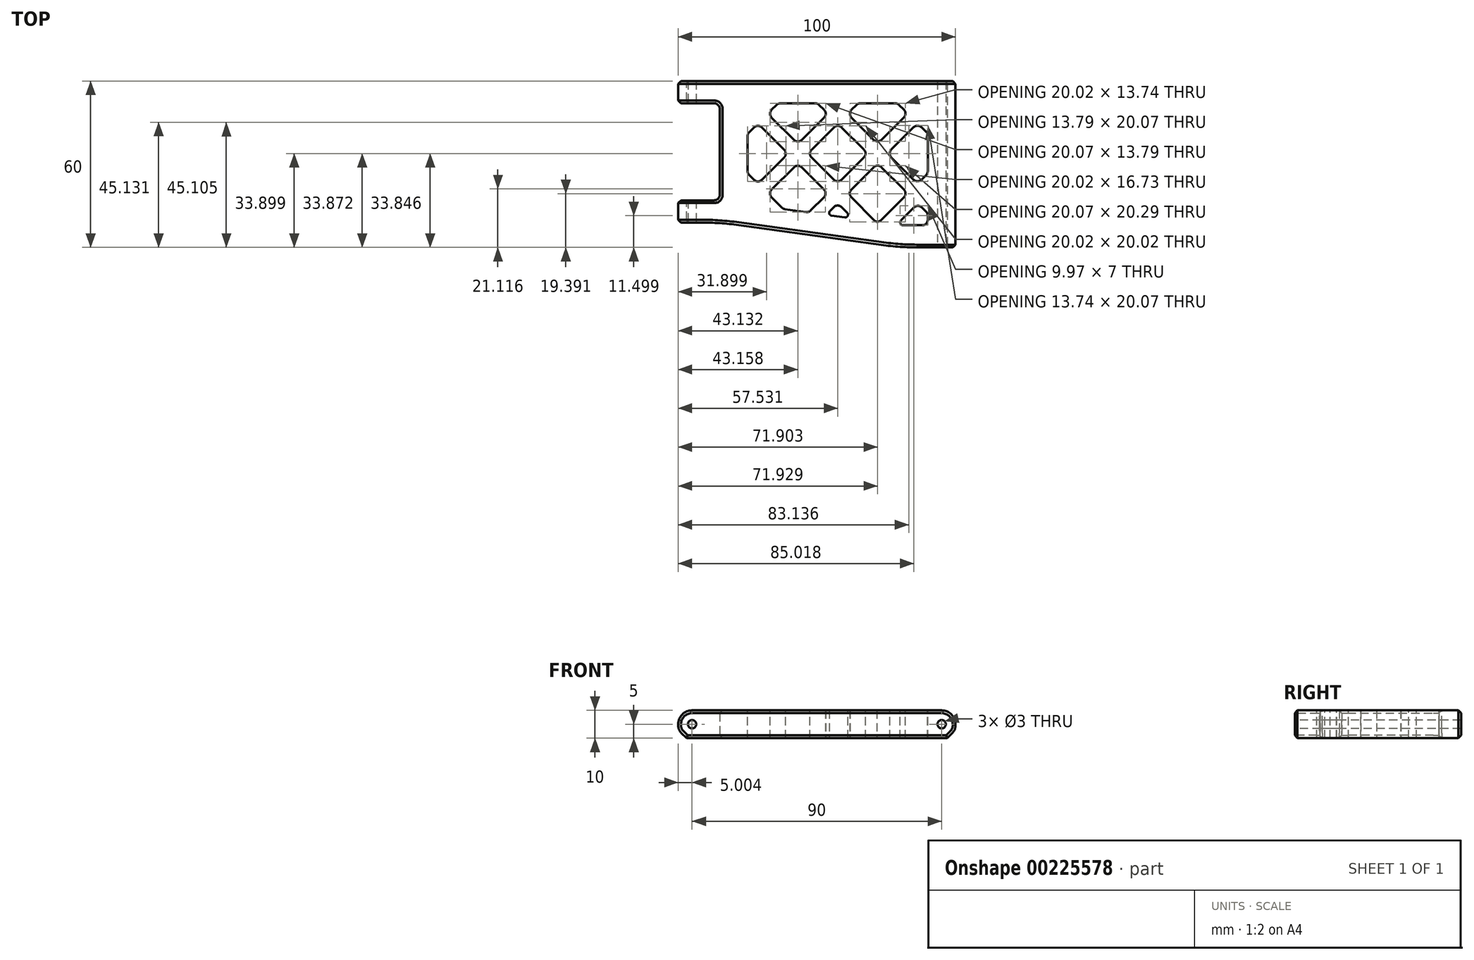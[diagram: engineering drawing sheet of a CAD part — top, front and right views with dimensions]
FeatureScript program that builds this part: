
annotation { "Feature Type Name" : "Feature", "Feature Type Description" : "" }
export const myFeature = defineFeature(function(context is Context, id is Id, definition is map)
    precondition{}
    {
        {
            var Q0;
            Q0=qCreatedBy(makeId("Top.planeOp"),FACE);
            var sketch = newSketch(context, id + "F0", { "sketchPlane" : qUnion([Q0])});
            skLineSegment(sketch, "E0", {"start": v(-37.98, 25.5) * mm, "end": v(-37.98, 17.5) * mm});
            skLineSegment(sketch, "E1", {"start": v(-37.98, 17.5) * mm, "end": v(-22.98, 17.5) * mm});
            skLineSegment(sketch, "E2", {"start": v(-22.98, 17.5) * mm, "end": v(-22.98, -17.5) * mm});
            skLineSegment(sketch, "E3", {"start": v(-22.98, -17.5) * mm, "end": v(-37.98, -17.5) * mm});
            skLineSegment(sketch, "E4", {"start": v(-37.98, -17.5) * mm, "end": v(-37.98, -25.5) * mm});
            skLineSegment(sketch, "E5", {"start": v(42.02, -34.5) * mm, "end": v(62.02, -34.5) * mm});
            skLineSegment(sketch, "E6", {"start": v(62.02, -34.5) * mm, "end": v(62.02, 25.5) * mm});
            skLineSegment(sketch, "E7", {"start": v(-37.98, -25.5) * mm, "end": v(-22.98, -25.5) * mm});
            skLineSegment(sketch, "E8", {"start": v(-22.98, -25.5) * mm, "end": v(42.02, -34.5) * mm});
            skLineSegment(sketch, "E9", {"start": v(-37.98, 25.5) * mm, "end": v(62.02, 25.5) * mm});
            skSolve(sketch);
        }
        {
            var Q0;
            Q0=makeQuery(id+"F0.imprint","IMPRINT",FACE,{"disambiguationData":[TD([[makeQuery(id+"F0.imprint","IMPRINT",EDGE,{"derivedFrom":sQuery(id+"F0.wireOp",EDGE,"E0")}),1.0]])]});
            extrude(context, id + "F1", {"entities" : qUnion([Q0]), "depth" : 10 * mm});
        }
        {
            var Q0;
            Q0=makeQuery(id+"F1.opExtrude","SWEPT_FACE",FACE,{"disambiguationData":[OSD([sQuery(id+"F0.wireOp",EDGE,"E7")])]});
            var sketch = newSketch(context, id + "F2", { "sketchPlane" : qUnion([Q0])});
            skCircle(sketch, "E10", {"center": v(-32.98, 5) * mm, "radius": 1.5 * mm});
            skPoint(sketch, "E10.centerSnap0", {"position": v(-22.98, 5) * mm});
            skSolve(sketch);
        }
        {
            var Q0;
            Q0=makeQuery(id+"F2.imprint","IMPRINT",FACE,{"disambiguationData":[TD([[makeQuery(id+"F2.imprint","IMPRINT",EDGE,{"derivedFrom":sQuery(id+"F2.wireOp",EDGE,"E10")}),1.0]])]});
            extrude(context, id + "F3", {"entities" : qUnion([Q0]), "operationType" : NewBodyOperationType.REMOVE, "endBound" : BoundingType.THROUGH_ALL, "oppositeDirection" : true, "depth" : 25 * mm});
        }
        {
            var Q0;
            Q0=makeQuery(id+"F1.opExtrude","CAP_FACE",FACE,{"disambiguationData":[OSD([sQuery(id+"F0.wireOp",EDGE,"E0"),sQuery(id+"F0.wireOp",EDGE,"E1"),sQuery(id+"F0.wireOp",EDGE,"E2"),sQuery(id+"F0.wireOp",EDGE,"E3"),sQuery(id+"F0.wireOp",EDGE,"E4"),sQuery(id+"F0.wireOp",EDGE,"E5"),sQuery(id+"F0.wireOp",EDGE,"E6"),sQuery(id+"F0.wireOp",EDGE,"BW3EDbzS-hKzO-ugTP-luI4-p5LjhiECR8vJ"),sQuery(id+"F0.wireOp",EDGE,"E7"),sQuery(id+"F0.wireOp",EDGE,"E8"),sQuery(id+"F0.wireOp",EDGE,"IeXmWBpi-uHs9-jreI-dXUk-5NaH1hiPgvdm"),sQuery(id+"F0.wireOp",EDGE,"tAyTVOHC-oCO1-Ys3H-gt9h-ad5hlT6EXF9F")])],"isStart":false});
            var sketch = newSketch(context, id + "F4", { "sketchPlane" : qUnion([Q0])});
            skLineSegment(sketch, "E11", {"start": v(-12.98, 17.5) * mm, "end": v(-12.98, -18.8) * mm});
            skLineSegment(sketch, "E12", {"start": v(-12.98, -18.8) * mm, "end": v(42.58, -26.5) * mm});
            skLineSegment(sketch, "E13", {"start": v(42.58, -26.5) * mm, "end": v(52.02, -26.5) * mm});
            skLineSegment(sketch, "E14", {"start": v(52.02, -26.5) * mm, "end": v(52.02, 17.5) * mm});
            skLineSegment(sketch, "E15", {"start": v(52.02, 17.5) * mm, "end": v(-12.98, 17.5) * mm});
            skLineSegment(sketch, "E16", {"start": v(48.49, 17.5) * mm, "end": v(9.12, -21.87) * mm});
            skLineSegment(sketch, "E17", {"start": v(52.02, 13.96) * mm, "end": v(15.33, -22.73) * mm});
            skLineSegment(sketch, "E18", {"start": v(-12.98, 13.96) * mm, "end": v(25.06, -24.08) * mm});
            skLineSegment(sketch, "E19", {"start": v(-9.44, 17.5) * mm, "end": v(33.27, -25.21) * mm});
            skLineSegment(sketch, "E20", {"start": v(-9.87, -19.24) * mm, "end": v(26.87, 17.5) * mm});
            skLineSegment(sketch, "E21", {"start": v(-12.98, -15.27) * mm, "end": v(19.8, 17.5) * mm});
            skLineSegment(sketch, "E22", {"start": v(52.02, -22.24) * mm, "end": v(12.29, 17.5) * mm});
            skLineSegment(sketch, "E23", {"start": v(52.02, -15.17) * mm, "end": v(19.36, 17.5) * mm});
            skLineSegment(sketch, "E24", {"start": v(-12.98, -7.76) * mm, "end": v(-0.15, -20.58) * mm});
            skLineSegment(sketch, "E25", {"start": v(-8.36, -19.45) * mm, "end": v(-12.98, -14.83) * mm});
            skLineSegment(sketch, "E26", {"start": v(41.08, 17.5) * mm, "end": v(52.02, 6.56) * mm});
            skLineSegment(sketch, "E27", {"start": v(44.79, -15) * mm, "end": v(34.42, -25.37) * mm});
            skLineSegment(sketch, "E28", {"start": v(44.79, -15) * mm, "end": v(52.02, -7.76) * mm});
            skLineSegment(sketch, "E29", {"start": v(40.87, -26.26) * mm, "end": v(52.02, -15.1) * mm});
            skLineSegment(sketch, "E30", {"start": v(-1.93, 17.5) * mm, "end": v(-12.98, 6.45) * mm});
            skSolve(sketch);
        }
        {
            var Q0;
            {var subQ0=sQuery(id+"F4.wireOp",EDGE,"E23");var subQ1=sQuery(id+"F4.wireOp",EDGE,"E14");var subQ2=makeQuery(id+"F4.imprint","INTERSECT",VERTEX,{"derivedFrom":[subQ1,subQ0]});Q0=makeQuery(id+"F4.imprint","IMPRINT",FACE,{"disambiguationData":[TD([[makeQuery(id+"F4.imprint","IMPRINT",EDGE,{"disambiguationData":[TD([[subQ2,-1.0]])],"derivedFrom":subQ1}),1.0]])]});}
            var Q1;
            {var subQ1=sQuery(id+"F4.wireOp",EDGE,"E13");Q1=makeQuery(id+"F4.imprint","IMPRINT",FACE,{"disambiguationData":[TD([[makeQuery(id+"F4.imprint","IMPRINT",EDGE,{"derivedFrom":subQ1}),1.0]])]});}
            var Q2;
            {var subQ0=sQuery(id+"F4.wireOp",EDGE,"E17");var subQ1=sQuery(id+"F4.wireOp",EDGE,"E12");var subQ2=makeQuery(id+"F4.imprint","INTERSECT",VERTEX,{"derivedFrom":[subQ1,subQ0]});Q2=makeQuery(id+"F4.imprint","IMPRINT",FACE,{"disambiguationData":[TD([[makeQuery(id+"F4.imprint","IMPRINT",EDGE,{"disambiguationData":[TD([[subQ2,-1.0]])],"derivedFrom":subQ1}),1.0]])]});}
            var Q3;
            {var subQ0=sQuery(id+"F4.wireOp",EDGE,"E22");var subQ1=sQuery(id+"F4.wireOp",EDGE,"E16");var subQ2=makeQuery(id+"F4.imprint","INTERSECT",VERTEX,{"derivedFrom":[subQ1,subQ0]});Q3=makeQuery(id+"F4.imprint","IMPRINT",FACE,{"disambiguationData":[TD([[makeQuery(id+"F4.imprint","IMPRINT",EDGE,{"disambiguationData":[TD([[subQ2,-1.0]])],"derivedFrom":subQ1}),-1.0]])]});}
            var Q4;
            {var subQ5=sQuery(id+"F4.wireOp",EDGE,"E16");var subQ7=sQuery(id+"F4.wireOp",EDGE,"E12");var subQ8=makeQuery(id+"F4.imprint","INTERSECT",VERTEX,{"derivedFrom":[subQ7,subQ5]});Q4=makeQuery(id+"F4.imprint","IMPRINT",FACE,{"disambiguationData":[TD([[makeQuery(id+"F4.imprint","IMPRINT",EDGE,{"disambiguationData":[TD([[subQ8,1.0]])],"derivedFrom":subQ7}),1.0]])]});}
            var Q5;
            {var subQ0=sQuery(id+"F4.wireOp",EDGE,"E24");var subQ1=sQuery(id+"F4.wireOp",EDGE,"E11");var subQ2=makeQuery(id+"F4.imprint","INTERSECT",VERTEX,{"derivedFrom":[subQ1,subQ0]});Q5=makeQuery(id+"F4.imprint","IMPRINT",FACE,{"disambiguationData":[TD([[makeQuery(id+"F4.imprint","IMPRINT",EDGE,{"disambiguationData":[TD([[subQ2,1.0]])],"derivedFrom":subQ1}),1.0]])]});}
            var Q6;
            {var subQ0=sQuery(id+"F4.wireOp",EDGE,"E22");var subQ1=sQuery(id+"F4.wireOp",EDGE,"E15");var subQ2=makeQuery(id+"F4.imprint","INTERSECT",VERTEX,{"derivedFrom":[subQ1,subQ0]});Q6=makeQuery(id+"F4.imprint","IMPRINT",FACE,{"disambiguationData":[TD([[makeQuery(id+"F4.imprint","IMPRINT",EDGE,{"disambiguationData":[TD([[subQ2,-1.0]])],"derivedFrom":subQ1}),1.0]])]});}
            var Q7;
            {var subQ0=sQuery(id+"F4.wireOp",EDGE,"E20");var subQ1=sQuery(id+"F4.wireOp",EDGE,"E15");var subQ2=makeQuery(id+"F4.imprint","INTERSECT",VERTEX,{"derivedFrom":[subQ1,subQ0]});Q7=makeQuery(id+"F4.imprint","IMPRINT",FACE,{"disambiguationData":[TD([[makeQuery(id+"F4.imprint","IMPRINT",EDGE,{"disambiguationData":[TD([[subQ2,1.0]])],"derivedFrom":subQ1}),1.0]])]});}
            var Q8;
            {var subQ0=sQuery(id+"F4.wireOp",EDGE,"E26");var subQ1=sQuery(id+"F4.wireOp",EDGE,"E14");var subQ2=makeQuery(id+"F4.imprint","INTERSECT",VERTEX,{"derivedFrom":[subQ1,subQ0]});Q8=makeQuery(id+"F4.imprint","IMPRINT",FACE,{"disambiguationData":[TD([[makeQuery(id+"F4.imprint","IMPRINT",EDGE,{"disambiguationData":[TD([[subQ2,1.0]])],"derivedFrom":subQ1}),1.0]])]});}
            var Q9;
            {var subQ5=sQuery(id+"F4.wireOp",EDGE,"E27");Q9=makeQuery(id+"F4.imprint","IMPRINT",FACE,{"disambiguationData":[TD([[makeQuery(id+"F4.imprint","IMPRINT",EDGE,{"derivedFrom":subQ5}),-1.0]])]});}
            var Q10;
            Q10=makeQuery(id+"F1.opExtrude","CAP_FACE",FACE,{"disambiguationData":[OSD([sQuery(id+"F0.wireOp",EDGE,"E0"),sQuery(id+"F0.wireOp",EDGE,"E1"),sQuery(id+"F0.wireOp",EDGE,"E2"),sQuery(id+"F0.wireOp",EDGE,"E3"),sQuery(id+"F0.wireOp",EDGE,"E4"),sQuery(id+"F0.wireOp",EDGE,"E5"),sQuery(id+"F0.wireOp",EDGE,"E6"),sQuery(id+"F0.wireOp",EDGE,"BW3EDbzS-hKzO-ugTP-luI4-p5LjhiECR8vJ"),sQuery(id+"F0.wireOp",EDGE,"E7"),sQuery(id+"F0.wireOp",EDGE,"E8"),sQuery(id+"F0.wireOp",EDGE,"IeXmWBpi-uHs9-jreI-dXUk-5NaH1hiPgvdm"),sQuery(id+"F0.wireOp",EDGE,"tAyTVOHC-oCO1-Ys3H-gt9h-ad5hlT6EXF9F")])],"isStart":true});
            extrude(context, id + "F5", {"entities" : qUnion([Q0, Q1, Q2, Q3, Q4, Q5, Q6, Q7, Q8, Q9]), "operationType" : NewBodyOperationType.REMOVE, "endBound" : BoundingType.UP_TO_SURFACE, "oppositeDirection" : true, "endBoundEntityFace" : qUnion([Q10]), "depth" : 25 * mm});
        }
        {
            var Q0;
            Q0=makeQuery(id+"F5.boolean.opBoolean","COPY",EDGE,{"derivedFrom":makeQuery(id+"F5.opExtrude","SWEPT_EDGE",EDGE,{"disambiguationData":[OSD([sQuery(id+"F4.wireOp",EDGE,"ZaEVg3SC-WDdr-0N1g-1CIV-3GaaaMJlVjN2"),sQuery(id+"F4.wireOp",EDGE,"i1amWwtg-wsxe-Ib75-jeaG-wsJk5hMrqHFT")])]})});
            var Q1;
            Q1=makeQuery(id+"F5.boolean.opBoolean","COPY",EDGE,{"derivedFrom":makeQuery(id+"F5.opExtrude","SWEPT_EDGE",EDGE,{"disambiguationData":[OSD([sQuery(id+"F4.wireOp",EDGE,"lIiY8wG4-uOwu-ETyX-0Y9X-0NFaVeheTsr8"),sQuery(id+"F4.wireOp",EDGE,"ifF4ALYo-uRmX-vEyd-hC4g-coADlhuvd4ly")])]})});
            var Q2;
            Q2=makeQuery(id+"F5.boolean.opBoolean","COPY",EDGE,{"derivedFrom":makeQuery(id+"F5.opExtrude","SWEPT_EDGE",EDGE,{"disambiguationData":[OSD([sQuery(id+"F4.wireOp",EDGE,"KTq638T6-onXi-3Qut-dIgx-5TcDHjVjb5bx"),sQuery(id+"F4.wireOp",EDGE,"lIiY8wG4-uOwu-ETyX-0Y9X-0NFaVeheTsr8")])]})});
            var Q3;
            Q3=makeQuery(id+"F5.boolean.opBoolean","COPY",EDGE,{"derivedFrom":makeQuery(id+"F5.opExtrude","SWEPT_EDGE",EDGE,{"disambiguationData":[OSD([sQuery(id+"F4.wireOp",EDGE,"adEcOkNO-EfV1-quEy-cv4m-vqoQPHR0sBr5"),sQuery(id+"F4.wireOp",EDGE,"FiieaGRp-roSN-Qhw9-YWAH-qJouDKNjpClN")])]})});
            var Q4;
            Q4=makeQuery(id+"F5.boolean.opBoolean","COPY",EDGE,{"derivedFrom":makeQuery(id+"F5.opExtrude","SWEPT_EDGE",EDGE,{"disambiguationData":[OSD([sQuery(id+"F4.wireOp",EDGE,"fQXT7rkZ-4DuX-Y0vK-KIZa-FyNlYHUYCe49"),sQuery(id+"F4.wireOp",EDGE,"i1amWwtg-wsxe-Ib75-jeaG-wsJk5hMrqHFT"),sQuery(id+"F4.wireOp",EDGE,"FiieaGRp-roSN-Qhw9-YWAH-qJouDKNjpClN")])]})});
            var Q5;
            Q5=makeQuery(id+"F5.boolean.opBoolean","COPY",EDGE,{"derivedFrom":makeQuery(id+"F5.opExtrude","SWEPT_EDGE",EDGE,{"disambiguationData":[OSD([sQuery(id+"F4.wireOp",EDGE,"fQXT7rkZ-4DuX-Y0vK-KIZa-FyNlYHUYCe49"),sQuery(id+"F4.wireOp",EDGE,"6CixbW05-UBlS-MQcj-7FzB-Ca1LVtebaFVZ")])]})});
            var Q6;
            Q6=makeQuery(id+"F5.boolean.opBoolean","COPY",EDGE,{"derivedFrom":makeQuery(id+"F5.opExtrude","SWEPT_EDGE",EDGE,{"disambiguationData":[OSD([sQuery(id+"F4.wireOp",EDGE,"lIiY8wG4-uOwu-ETyX-0Y9X-0NFaVeheTsr8"),sQuery(id+"F4.wireOp",EDGE,"fQXT7rkZ-4DuX-Y0vK-KIZa-FyNlYHUYCe49")])]})});
            var Q7;
            Q7=makeQuery(id+"F5.boolean.opBoolean","COPY",EDGE,{"derivedFrom":makeQuery(id+"F5.opExtrude","SWEPT_EDGE",EDGE,{"disambiguationData":[OSD([sQuery(id+"F4.wireOp",EDGE,"lIiY8wG4-uOwu-ETyX-0Y9X-0NFaVeheTsr8"),sQuery(id+"F4.wireOp",EDGE,"FiieaGRp-roSN-Qhw9-YWAH-qJouDKNjpClN")])]})});
            var Q8;
            Q8=makeQuery(id+"F5.boolean.opBoolean","COPY",EDGE,{"derivedFrom":makeQuery(id+"F5.opExtrude","SWEPT_EDGE",EDGE,{"disambiguationData":[OSD([sQuery(id+"F4.wireOp",EDGE,"QQoZa2y4-lnB9-MFLh-E48C-Qh8QXVeHaOTo"),sQuery(id+"F4.wireOp",EDGE,"6CixbW05-UBlS-MQcj-7FzB-Ca1LVtebaFVZ")])]})});
            var Q9;
            Q9=makeQuery(id+"F5.boolean.opBoolean","COPY",EDGE,{"derivedFrom":makeQuery(id+"F5.opExtrude","SWEPT_EDGE",EDGE,{"disambiguationData":[OSD([sQuery(id+"F4.wireOp",EDGE,"PUbkOMFc-aEfS-HhHo-NWSC-wt2yRkt3aVop"),sQuery(id+"F4.wireOp",EDGE,"adEcOkNO-EfV1-quEy-cv4m-vqoQPHR0sBr5")])]})});
            var Q10;
            Q10=makeQuery(id+"F5.boolean.opBoolean","COPY",EDGE,{"derivedFrom":makeQuery(id+"F5.opExtrude","SWEPT_EDGE",EDGE,{"disambiguationData":[OSD([sQuery(id+"F4.wireOp",EDGE,"u151USCK-d2Jm-vOpM-AoZG-Gq13jmKxo3bC"),sQuery(id+"F4.wireOp",EDGE,"ZaEVg3SC-WDdr-0N1g-1CIV-3GaaaMJlVjN2")])]})});
            var Q11;
            Q11=makeQuery(id+"F5.boolean.opBoolean","COPY",EDGE,{"derivedFrom":makeQuery(id+"F5.opExtrude","SWEPT_EDGE",EDGE,{"disambiguationData":[OSD([sQuery(id+"F4.wireOp",EDGE,"PUbkOMFc-aEfS-HhHo-NWSC-wt2yRkt3aVop"),sQuery(id+"F4.wireOp",EDGE,"CK30QNie-qYM8-a8fS-8cOY-rL2En2E0fWi0")])]})});
            var Q12;
            Q12=makeQuery(id+"F5.boolean.opBoolean","COPY",EDGE,{"derivedFrom":makeQuery(id+"F5.opExtrude","SWEPT_EDGE",EDGE,{"disambiguationData":[OSD([sQuery(id+"F4.wireOp",EDGE,"QQoZa2y4-lnB9-MFLh-E48C-Qh8QXVeHaOTo"),sQuery(id+"F4.wireOp",EDGE,"u151USCK-d2Jm-vOpM-AoZG-Gq13jmKxo3bC")])]})});
            var Q13;
            Q13=makeQuery(id+"F5.boolean.opBoolean","COPY",EDGE,{"derivedFrom":makeQuery(id+"F5.opExtrude","SWEPT_EDGE",EDGE,{"disambiguationData":[OSD([sQuery(id+"F4.wireOp",EDGE,"PUbkOMFc-aEfS-HhHo-NWSC-wt2yRkt3aVop"),sQuery(id+"F4.wireOp",EDGE,"tCY4romA-bLon-Adh6-hAWd-4SXAEG81LoxB")])]})});
            var Q14;
            Q14=makeQuery(id+"F5.boolean.opBoolean","COPY",EDGE,{"derivedFrom":makeQuery(id+"F5.opExtrude","SWEPT_EDGE",EDGE,{"disambiguationData":[OSD([sQuery(id+"F4.wireOp",EDGE,"tCY4romA-bLon-Adh6-hAWd-4SXAEG81LoxB"),sQuery(id+"F4.wireOp",EDGE,"4gVtD0sa-nhfM-sN6f-blQz-uG5Zat8Q9Qrc")])]})});
            var Q15;
            Q15=makeQuery(id+"F5.boolean.opBoolean","COPY",EDGE,{"derivedFrom":makeQuery(id+"F5.opExtrude","SWEPT_EDGE",EDGE,{"disambiguationData":[OSD([sQuery(id+"F4.wireOp",EDGE,"QQoZa2y4-lnB9-MFLh-E48C-Qh8QXVeHaOTo"),sQuery(id+"F4.wireOp",EDGE,"xG4hkh3S-L24H-y6HB-11TF-rizkPmb2XNVC")])]})});
            var Q16;
            Q16=makeQuery(id+"F5.boolean.opBoolean","COPY",EDGE,{"derivedFrom":makeQuery(id+"F5.opExtrude","SWEPT_EDGE",EDGE,{"disambiguationData":[OSD([sQuery(id+"F4.wireOp",EDGE,"u151USCK-d2Jm-vOpM-AoZG-Gq13jmKxo3bC"),sQuery(id+"F4.wireOp",EDGE,"xG4hkh3S-L24H-y6HB-11TF-rizkPmb2XNVC")])]})});
            var Q17;
            Q17=makeQuery(id+"F5.boolean.opBoolean","COPY",EDGE,{"derivedFrom":makeQuery(id+"F5.opExtrude","SWEPT_EDGE",EDGE,{"disambiguationData":[OSD([sQuery(id+"F4.wireOp",EDGE,"tCY4romA-bLon-Adh6-hAWd-4SXAEG81LoxB"),sQuery(id+"F4.wireOp",EDGE,"CK30QNie-qYM8-a8fS-8cOY-rL2En2E0fWi0"),sQuery(id+"F4.wireOp",EDGE,"ZaEVg3SC-WDdr-0N1g-1CIV-3GaaaMJlVjN2")])]})});
            var Q18;
            Q18=makeQuery(id+"F5.boolean.opBoolean","COPY",EDGE,{"derivedFrom":makeQuery(id+"F5.opExtrude","SWEPT_EDGE",EDGE,{"disambiguationData":[OSD([sQuery(id+"F4.wireOp",EDGE,"UHvlroPN-YfBx-vEqm-jT0p-LSI2mjvl9sd3"),sQuery(id+"F4.wireOp",EDGE,"4gVtD0sa-nhfM-sN6f-blQz-uG5Zat8Q9Qrc")])]})});
            var Q19;
            Q19=makeQuery(id+"F5.boolean.opBoolean","COPY",EDGE,{"derivedFrom":makeQuery(id+"F5.opExtrude","SWEPT_EDGE",EDGE,{"disambiguationData":[OSD([sQuery(id+"F4.wireOp",EDGE,"UHvlroPN-YfBx-vEqm-jT0p-LSI2mjvl9sd3"),sQuery(id+"F4.wireOp",EDGE,"tCY4romA-bLon-Adh6-hAWd-4SXAEG81LoxB")])]})});
            var Q20;
            Q20=makeQuery(id+"F1.opExtrude","SWEPT_EDGE",EDGE,{"disambiguationData":[OSD([sQuery(id+"F0.wireOp",EDGE,"E1"),sQuery(id+"F0.wireOp",EDGE,"E2")])]});
            var Q21;
            Q21=makeQuery(id+"F1.opExtrude","SWEPT_EDGE",EDGE,{"disambiguationData":[OSD([sQuery(id+"F0.wireOp",EDGE,"E2"),sQuery(id+"F0.wireOp",EDGE,"E3")])]});
            fillet(context, id + "F6", {"entities" : qUnion([Q0, Q1, Q2, Q3, Q4, Q5, Q6, Q7, Q8, Q9, Q10, Q11, Q12, Q13, Q14, Q15, Q16, Q17, Q18, Q19, Q20, Q21]), "radius" : 2 * mm, "tangentPropagation" : true, "allowEdgeOverflow" : false});
        }
        {
            var Q0;
            Q0=makeQuery(id+"F1.opExtrude","CAP_EDGE",EDGE,{"disambiguationData":[OSD([sQuery(id+"F0.wireOp",EDGE,"E0")])],"isStart":false});
            var Q1;
            Q1=makeQuery(id+"F1.opExtrude","CAP_EDGE",EDGE,{"disambiguationData":[OSD([sQuery(id+"F0.wireOp",EDGE,"E4")])],"isStart":false});
            var Q2;
            Q2=makeQuery(id+"F1.opExtrude","CAP_EDGE",EDGE,{"disambiguationData":[OSD([sQuery(id+"F0.wireOp",EDGE,"E6")])],"isStart":false});
            fillet(context, id + "F7", {"entities" : qUnion([Q0, Q1, Q2]), "radius" : 5 * mm, "tangentPropagation" : true, "allowEdgeOverflow" : false});
        }
        {
            var Q0;
            Q0=makeQuery(id+"F1.opExtrude","CAP_EDGE",EDGE,{"disambiguationData":[OSD([sQuery(id+"F0.wireOp",EDGE,"E4")])],"isStart":true});
            var Q1;
            Q1=makeQuery(id+"F1.opExtrude","CAP_EDGE",EDGE,{"disambiguationData":[OSD([sQuery(id+"F0.wireOp",EDGE,"E0")])],"isStart":true});
            var Q2;
            Q2=makeQuery(id+"F1.opExtrude","CAP_EDGE",EDGE,{"disambiguationData":[OSD([sQuery(id+"F0.wireOp",EDGE,"E6")])],"isStart":true});
            chamfer(context, id + "F8", {"entities" : qUnion([Q0, Q1, Q2]), "width" : 3 * mm, "tangentPropagation" : true});
        }
        {
            var Q0;
            {var subQ0=sQuery(id+"F0.wireOp",EDGE,"E6");Q0=makeQuery(id+"F8.opChamfer","BLEND_EDGE",EDGE,{"blendedFrom":[makeQuery(id+"F1.opExtrude","CAP_EDGE",EDGE,{"disambiguationData":[OSD([subQ0])],"isStart":true}),makeQuery(id+"F1.opExtrude","SWEPT_FACE",FACE,{"disambiguationData":[OSD([subQ0])]})],"blendedInto":[makeQuery(id+"F1.opExtrude","SWEPT_FACE",FACE,{"disambiguationData":[OSD([subQ0])]})]});}
            var Q1;
            {var subQ0=sQuery(id+"F0.wireOp",EDGE,"E4");Q1=makeQuery(id+"F8.opChamfer","BLEND_EDGE",EDGE,{"blendedFrom":[makeQuery(id+"F1.opExtrude","CAP_EDGE",EDGE,{"disambiguationData":[OSD([subQ0])],"isStart":true}),makeQuery(id+"F1.opExtrude","SWEPT_FACE",FACE,{"disambiguationData":[OSD([subQ0])]})],"blendedInto":[makeQuery(id+"F1.opExtrude","SWEPT_FACE",FACE,{"disambiguationData":[OSD([subQ0])]})]});}
            var Q2;
            {var subQ0=sQuery(id+"F0.wireOp",EDGE,"E0");Q2=makeQuery(id+"F8.opChamfer","BLEND_EDGE",EDGE,{"blendedFrom":[makeQuery(id+"F1.opExtrude","CAP_EDGE",EDGE,{"disambiguationData":[OSD([subQ0])],"isStart":true}),makeQuery(id+"F1.opExtrude","SWEPT_FACE",FACE,{"disambiguationData":[OSD([subQ0])]})],"blendedInto":[makeQuery(id+"F1.opExtrude","SWEPT_FACE",FACE,{"disambiguationData":[OSD([subQ0])]})]});}
            fillet(context, id + "F9", {"entities" : qUnion([Q0, Q1, Q2]), "radius" : 4 * mm, "tangentPropagation" : true, "allowEdgeOverflow" : false});
        }
        {
            var Q0;
            Q0=makeQuery(id+"F1.opExtrude","SWEPT_EDGE",EDGE,{"disambiguationData":[OSD([sQuery(id+"F0.wireOp",EDGE,"E7"),sQuery(id+"F0.wireOp",EDGE,"E8")])]});
            var Q1;
            Q1=makeQuery(id+"F1.opExtrude","SWEPT_EDGE",EDGE,{"disambiguationData":[OSD([sQuery(id+"F0.wireOp",EDGE,"IeXmWBpi-uHs9-jreI-dXUk-5NaH1hiPgvdm"),sQuery(id+"F0.wireOp",EDGE,"tAyTVOHC-oCO1-Ys3H-gt9h-ad5hlT6EXF9F")])]});
            var Q2;
            Q2=makeQuery(id+"F1.opExtrude","SWEPT_EDGE",EDGE,{"disambiguationData":[OSD([sQuery(id+"F0.wireOp",EDGE,"BW3EDbzS-hKzO-ugTP-luI4-p5LjhiECR8vJ"),sQuery(id+"F0.wireOp",EDGE,"tAyTVOHC-oCO1-Ys3H-gt9h-ad5hlT6EXF9F")])]});
            var Q3;
            Q3=makeQuery(id+"F1.opExtrude","SWEPT_EDGE",EDGE,{"disambiguationData":[OSD([sQuery(id+"F0.wireOp",EDGE,"E5"),sQuery(id+"F0.wireOp",EDGE,"E8")])]});
            fillet(context, id + "F10", {"entities" : qUnion([Q0, Q1, Q2, Q3]), "radius" : 100 * mm, "allowEdgeOverflow" : false});
        }
        {
            var Q0;
            Q0=makeQuery(id+"F1.opExtrude","SWEPT_FACE",FACE,{"disambiguationData":[OSD([sQuery(id+"F0.wireOp",EDGE,"E5")])]});
            var sketch = newSketch(context, id + "F11", { "sketchPlane" : qUnion([Q0])});
            skCircle(sketch, "E31", {"center": v(57.02, 5) * mm, "radius": 1.5 * mm});
            skPoint(sketch, "E31.centerSnap0", {"position": v(48.91, 5) * mm});
            skSolve(sketch);
        }
        {
            var Q0;
            Q0=makeQuery(id+"F11.imprint","IMPRINT",FACE,{"disambiguationData":[TD([[makeQuery(id+"F11.imprint","IMPRINT",EDGE,{"derivedFrom":sQuery(id+"F11.wireOp",EDGE,"E31")}),1.0]])]});
            extrude(context, id + "F12", {"entities" : qUnion([Q0]), "operationType" : NewBodyOperationType.REMOVE, "endBound" : BoundingType.THROUGH_ALL, "oppositeDirection" : true, "depth" : 25 * mm});
        }
        {
            var Q0;
            {var subQ0=sQuery(id+"F0.wireOp",EDGE,"E8");var subQ1=sQuery(id+"F0.wireOp",EDGE,"E7");Q0=makeQuery(id+"F10.opFillet","BLEND_EDGE",EDGE,{"blendedFrom":[makeQuery(id+"F1.opExtrude","SWEPT_EDGE",EDGE,{"disambiguationData":[OSD([subQ1,subQ0])]}),makeQuery(id+"F1.opExtrude","CAP_FACE",FACE,{"disambiguationData":[OSD([sQuery(id+"F0.wireOp",EDGE,"E0"),sQuery(id+"F0.wireOp",EDGE,"E1"),sQuery(id+"F0.wireOp",EDGE,"E2"),sQuery(id+"F0.wireOp",EDGE,"E3"),sQuery(id+"F0.wireOp",EDGE,"E4"),sQuery(id+"F0.wireOp",EDGE,"E5"),sQuery(id+"F0.wireOp",EDGE,"E6"),sQuery(id+"F0.wireOp",EDGE,"BW3EDbzS-hKzO-ugTP-luI4-p5LjhiECR8vJ"),subQ1,subQ0,sQuery(id+"F0.wireOp",EDGE,"IeXmWBpi-uHs9-jreI-dXUk-5NaH1hiPgvdm"),sQuery(id+"F0.wireOp",EDGE,"tAyTVOHC-oCO1-Ys3H-gt9h-ad5hlT6EXF9F")])],"isStart":false})],"blendedInto":[makeQuery(id+"F1.opExtrude","CAP_FACE",FACE,{"disambiguationData":[OSD([sQuery(id+"F0.wireOp",EDGE,"E0"),sQuery(id+"F0.wireOp",EDGE,"E1"),sQuery(id+"F0.wireOp",EDGE,"E2"),sQuery(id+"F0.wireOp",EDGE,"E3"),sQuery(id+"F0.wireOp",EDGE,"E4"),sQuery(id+"F0.wireOp",EDGE,"E5"),sQuery(id+"F0.wireOp",EDGE,"E6"),sQuery(id+"F0.wireOp",EDGE,"BW3EDbzS-hKzO-ugTP-luI4-p5LjhiECR8vJ"),subQ1,subQ0,sQuery(id+"F0.wireOp",EDGE,"IeXmWBpi-uHs9-jreI-dXUk-5NaH1hiPgvdm"),sQuery(id+"F0.wireOp",EDGE,"tAyTVOHC-oCO1-Ys3H-gt9h-ad5hlT6EXF9F")])],"isStart":false})]});}
            var Q1;
            Q1=makeQuery(id+"F1.opExtrude","CAP_EDGE",EDGE,{"disambiguationData":[OSD([sQuery(id+"F0.wireOp",EDGE,"E7")])],"isStart":true});
            var Q2;
            Q2=makeQuery(id+"F1.opExtrude","CAP_EDGE",EDGE,{"disambiguationData":[OSD([sQuery(id+"F0.wireOp",EDGE,"IeXmWBpi-uHs9-jreI-dXUk-5NaH1hiPgvdm")])],"isStart":true});
            var Q3;
            Q3=makeQuery(id+"F1.opExtrude","CAP_EDGE",EDGE,{"disambiguationData":[OSD([sQuery(id+"F0.wireOp",EDGE,"E1")])],"isStart":true});
            var Q4;
            Q4=makeQuery(id+"F1.opExtrude","CAP_EDGE",EDGE,{"disambiguationData":[OSD([sQuery(id+"F0.wireOp",EDGE,"E2")])],"isStart":false});
            var Q5;
            Q5=makeQuery(id+"F1.opExtrude","CAP_EDGE",EDGE,{"disambiguationData":[OSD([sQuery(id+"F0.wireOp",EDGE,"tAyTVOHC-oCO1-Ys3H-gt9h-ad5hlT6EXF9F")])],"isStart":false});
            chamfer(context, id + "F13", {"entities" : qUnion([Q0, Q1, Q2, Q3, Q4, Q5]), "width" : 1 * mm, "tangentPropagation" : true});
        }
        {
            var Q0;
            Q0=makeQuery(id+"F5.boolean.opBoolean","COPY",EDGE,{"derivedFrom":makeQuery(id+"F5.opExtrude","SWEPT_EDGE",EDGE,{"disambiguationData":[OSD([sQuery(id+"F4.wireOp",EDGE,"E15"),sQuery(id+"F4.wireOp",EDGE,"E30")])]})});
            var Q1;
            Q1=makeQuery(id+"F5.boolean.opBoolean","COPY",EDGE,{"derivedFrom":makeQuery(id+"F5.opExtrude","SWEPT_EDGE",EDGE,{"disambiguationData":[OSD([sQuery(id+"F4.wireOp",EDGE,"E19"),sQuery(id+"F4.wireOp",EDGE,"E30")])]})});
            var Q2;
            Q2=makeQuery(id+"F5.boolean.opBoolean","COPY",EDGE,{"derivedFrom":makeQuery(id+"F5.opExtrude","SWEPT_EDGE",EDGE,{"disambiguationData":[OSD([sQuery(id+"F4.wireOp",EDGE,"E18"),sQuery(id+"F4.wireOp",EDGE,"E30")])]})});
            var Q3;
            Q3=makeQuery(id+"F5.boolean.opBoolean","COPY",EDGE,{"derivedFrom":makeQuery(id+"F5.opExtrude","SWEPT_EDGE",EDGE,{"disambiguationData":[OSD([sQuery(id+"F4.wireOp",EDGE,"E11"),sQuery(id+"F4.wireOp",EDGE,"E30")])]})});
            var Q4;
            Q4=makeQuery(id+"F5.boolean.opBoolean","COPY",EDGE,{"derivedFrom":makeQuery(id+"F5.opExtrude","SWEPT_EDGE",EDGE,{"disambiguationData":[OSD([sQuery(id+"F4.wireOp",EDGE,"E11"),sQuery(id+"F4.wireOp",EDGE,"E24")])]})});
            var Q5;
            Q5=makeQuery(id+"F5.boolean.opBoolean","COPY",EDGE,{"derivedFrom":makeQuery(id+"F5.opExtrude","SWEPT_EDGE",EDGE,{"disambiguationData":[OSD([sQuery(id+"F4.wireOp",EDGE,"E21"),sQuery(id+"F4.wireOp",EDGE,"E24")])]})});
            var Q6;
            Q6=makeQuery(id+"F5.boolean.opBoolean","COPY",EDGE,{"derivedFrom":makeQuery(id+"F5.opExtrude","SWEPT_EDGE",EDGE,{"disambiguationData":[OSD([sQuery(id+"F4.wireOp",EDGE,"E18"),sQuery(id+"F4.wireOp",EDGE,"E21")])]})});
            var Q7;
            Q7=makeQuery(id+"F5.boolean.opBoolean","COPY",EDGE,{"derivedFrom":makeQuery(id+"F5.opExtrude","SWEPT_EDGE",EDGE,{"disambiguationData":[OSD([sQuery(id+"F4.wireOp",EDGE,"E19"),sQuery(id+"F4.wireOp",EDGE,"E21")])]})});
            var Q8;
            Q8=makeQuery(id+"F5.boolean.opBoolean","COPY",EDGE,{"derivedFrom":makeQuery(id+"F5.opExtrude","SWEPT_EDGE",EDGE,{"disambiguationData":[OSD([sQuery(id+"F4.wireOp",EDGE,"E21"),sQuery(id+"F4.wireOp",EDGE,"E22")])]})});
            var Q9;
            Q9=makeQuery(id+"F5.boolean.opBoolean","COPY",EDGE,{"derivedFrom":makeQuery(id+"F5.opExtrude","SWEPT_EDGE",EDGE,{"disambiguationData":[OSD([sQuery(id+"F4.wireOp",EDGE,"E15"),sQuery(id+"F4.wireOp",EDGE,"E22")])]})});
            var Q10;
            Q10=makeQuery(id+"F5.boolean.opBoolean","COPY",EDGE,{"derivedFrom":makeQuery(id+"F5.opExtrude","SWEPT_EDGE",EDGE,{"disambiguationData":[OSD([sQuery(id+"F4.wireOp",EDGE,"E20"),sQuery(id+"F4.wireOp",EDGE,"E24")])]})});
            var Q11;
            Q11=makeQuery(id+"F5.boolean.opBoolean","COPY",EDGE,{"derivedFrom":makeQuery(id+"F5.opExtrude","SWEPT_EDGE",EDGE,{"disambiguationData":[OSD([sQuery(id+"F4.wireOp",EDGE,"E12"),sQuery(id+"F4.wireOp",EDGE,"E24")])]})});
            var Q12;
            Q12=makeQuery(id+"F5.boolean.opBoolean","COPY",EDGE,{"derivedFrom":makeQuery(id+"F5.opExtrude","SWEPT_EDGE",EDGE,{"disambiguationData":[OSD([sQuery(id+"F4.wireOp",EDGE,"E12"),sQuery(id+"F4.wireOp",EDGE,"E16")])]})});
            var Q13;
            Q13=makeQuery(id+"F5.boolean.opBoolean","COPY",EDGE,{"derivedFrom":makeQuery(id+"F5.opExtrude","SWEPT_EDGE",EDGE,{"disambiguationData":[OSD([sQuery(id+"F4.wireOp",EDGE,"E16"),sQuery(id+"F4.wireOp",EDGE,"E18")])]})});
            var Q14;
            Q14=makeQuery(id+"F5.boolean.opBoolean","COPY",EDGE,{"derivedFrom":makeQuery(id+"F5.opExtrude","SWEPT_EDGE",EDGE,{"disambiguationData":[OSD([sQuery(id+"F4.wireOp",EDGE,"E18"),sQuery(id+"F4.wireOp",EDGE,"E20")])]})});
            var Q15;
            Q15=makeQuery(id+"F5.boolean.opBoolean","COPY",EDGE,{"derivedFrom":makeQuery(id+"F5.opExtrude","SWEPT_EDGE",EDGE,{"disambiguationData":[OSD([sQuery(id+"F4.wireOp",EDGE,"E20"),sQuery(id+"F4.wireOp",EDGE,"E22")])]})});
            var Q16;
            Q16=makeQuery(id+"F5.boolean.opBoolean","COPY",EDGE,{"derivedFrom":makeQuery(id+"F5.opExtrude","SWEPT_EDGE",EDGE,{"disambiguationData":[OSD([sQuery(id+"F4.wireOp",EDGE,"E15"),sQuery(id+"F4.wireOp",EDGE,"E20")])]})});
            var Q17;
            Q17=makeQuery(id+"F5.boolean.opBoolean","COPY",EDGE,{"derivedFrom":makeQuery(id+"F5.opExtrude","SWEPT_EDGE",EDGE,{"disambiguationData":[OSD([sQuery(id+"F4.wireOp",EDGE,"E17"),sQuery(id+"F4.wireOp",EDGE,"E22")])]})});
            var Q18;
            Q18=makeQuery(id+"F5.boolean.opBoolean","COPY",EDGE,{"derivedFrom":makeQuery(id+"F5.opExtrude","SWEPT_EDGE",EDGE,{"disambiguationData":[OSD([sQuery(id+"F4.wireOp",EDGE,"E17"),sQuery(id+"F4.wireOp",EDGE,"E26")])]})});
            var Q19;
            Q19=makeQuery(id+"F5.boolean.opBoolean","COPY",EDGE,{"derivedFrom":makeQuery(id+"F5.opExtrude","SWEPT_EDGE",EDGE,{"disambiguationData":[OSD([sQuery(id+"F4.wireOp",EDGE,"E22"),sQuery(id+"F4.wireOp",EDGE,"E29")])]})});
            var Q20;
            Q20=makeQuery(id+"F5.boolean.opBoolean","COPY",EDGE,{"derivedFrom":makeQuery(id+"F5.opExtrude","SWEPT_EDGE",EDGE,{"disambiguationData":[OSD([sQuery(id+"F4.wireOp",EDGE,"E15"),sQuery(id+"F4.wireOp",EDGE,"E26")])]})});
            var Q21;
            Q21=makeQuery(id+"F5.boolean.opBoolean","COPY",EDGE,{"derivedFrom":makeQuery(id+"F5.opExtrude","SWEPT_EDGE",EDGE,{"disambiguationData":[OSD([sQuery(id+"F4.wireOp",EDGE,"E16"),sQuery(id+"F4.wireOp",EDGE,"E19")])]})});
            var Q22;
            Q22=makeQuery(id+"F5.boolean.opBoolean","COPY",EDGE,{"derivedFrom":makeQuery(id+"F5.opExtrude","SWEPT_EDGE",EDGE,{"disambiguationData":[OSD([sQuery(id+"F4.wireOp",EDGE,"E12"),sQuery(id+"F4.wireOp",EDGE,"E19")])]})});
            var Q23;
            Q23=makeQuery(id+"F5.boolean.opBoolean","COPY",EDGE,{"derivedFrom":makeQuery(id+"F5.opExtrude","SWEPT_EDGE",EDGE,{"disambiguationData":[OSD([sQuery(id+"F4.wireOp",EDGE,"E12"),sQuery(id+"F4.wireOp",EDGE,"E27")])]})});
            var Q24;
            Q24=makeQuery(id+"F5.boolean.opBoolean","COPY",EDGE,{"derivedFrom":makeQuery(id+"F5.opExtrude","SWEPT_EDGE",EDGE,{"disambiguationData":[OSD([sQuery(id+"F4.wireOp",EDGE,"E13"),sQuery(id+"F4.wireOp",EDGE,"E14")])]})});
            var Q25;
            Q25=makeQuery(id+"F5.boolean.opBoolean","COPY",EDGE,{"derivedFrom":makeQuery(id+"F5.opExtrude","SWEPT_EDGE",EDGE,{"disambiguationData":[OSD([sQuery(id+"F4.wireOp",EDGE,"E14"),sQuery(id+"F4.wireOp",EDGE,"E28")])]})});
            var Q26;
            Q26=makeQuery(id+"F5.boolean.opBoolean","COPY",EDGE,{"derivedFrom":makeQuery(id+"F5.opExtrude","SWEPT_EDGE",EDGE,{"disambiguationData":[OSD([sQuery(id+"F4.wireOp",EDGE,"E23"),sQuery(id+"F4.wireOp",EDGE,"E28")])]})});
            var Q27;
            Q27=makeQuery(id+"F5.boolean.opBoolean","COPY",EDGE,{"derivedFrom":makeQuery(id+"F5.opExtrude","SWEPT_EDGE",EDGE,{"disambiguationData":[OSD([sQuery(id+"F4.wireOp",EDGE,"E16"),sQuery(id+"F4.wireOp",EDGE,"E23")])]})});
            var Q28;
            Q28=makeQuery(id+"F5.boolean.opBoolean","COPY",EDGE,{"derivedFrom":makeQuery(id+"F5.opExtrude","SWEPT_EDGE",EDGE,{"disambiguationData":[OSD([sQuery(id+"F4.wireOp",EDGE,"E16"),sQuery(id+"F4.wireOp",EDGE,"E26")])]})});
            var Q29;
            Q29=makeQuery(id+"F5.boolean.opBoolean","COPY",EDGE,{"derivedFrom":makeQuery(id+"F5.opExtrude","SWEPT_EDGE",EDGE,{"disambiguationData":[OSD([sQuery(id+"F4.wireOp",EDGE,"E16"),sQuery(id+"F4.wireOp",EDGE,"E22")])]})});
            var Q30;
            Q30=makeQuery(id+"F5.boolean.opBoolean","COPY",EDGE,{"derivedFrom":makeQuery(id+"F5.opExtrude","SWEPT_EDGE",EDGE,{"disambiguationData":[OSD([sQuery(id+"F4.wireOp",EDGE,"E22"),sQuery(id+"F4.wireOp",EDGE,"E27"),sQuery(id+"F4.wireOp",EDGE,"E28")])]})});
            var Q31;
            Q31=makeQuery(id+"F5.boolean.opBoolean","COPY",EDGE,{"derivedFrom":makeQuery(id+"F5.opExtrude","SWEPT_EDGE",EDGE,{"disambiguationData":[OSD([sQuery(id+"F4.wireOp",EDGE,"E17"),sQuery(id+"F4.wireOp",EDGE,"E19")])]})});
            var Q32;
            Q32=makeQuery(id+"F5.boolean.opBoolean","COPY",EDGE,{"derivedFrom":makeQuery(id+"F5.opExtrude","SWEPT_EDGE",EDGE,{"disambiguationData":[OSD([sQuery(id+"F4.wireOp",EDGE,"E19"),sQuery(id+"F4.wireOp",EDGE,"E20")])]})});
            var Q33;
            Q33=makeQuery(id+"F5.boolean.opBoolean","COPY",EDGE,{"derivedFrom":makeQuery(id+"F5.opExtrude","SWEPT_EDGE",EDGE,{"disambiguationData":[OSD([sQuery(id+"F4.wireOp",EDGE,"E17"),sQuery(id+"F4.wireOp",EDGE,"E18")])]})});
            var Q34;
            Q34=makeQuery(id+"F5.boolean.opBoolean","COPY",EDGE,{"derivedFrom":makeQuery(id+"F5.opExtrude","SWEPT_EDGE",EDGE,{"disambiguationData":[OSD([sQuery(id+"F4.wireOp",EDGE,"E20"),sQuery(id+"F4.wireOp",EDGE,"E23")])]})});
            var Q35;
            Q35=makeQuery(id+"F5.boolean.opBoolean","COPY",EDGE,{"derivedFrom":makeQuery(id+"F5.opExtrude","SWEPT_EDGE",EDGE,{"disambiguationData":[OSD([sQuery(id+"F4.wireOp",EDGE,"E14"),sQuery(id+"F4.wireOp",EDGE,"E22")])]})});
            var Q36;
            Q36=makeQuery(id+"F5.boolean.opBoolean","COPY",EDGE,{"derivedFrom":makeQuery(id+"F5.opExtrude","SWEPT_EDGE",EDGE,{"disambiguationData":[OSD([sQuery(id+"F4.wireOp",EDGE,"E17"),sQuery(id+"F4.wireOp",EDGE,"E23")])]})});
            fillet(context, id + "F14", {"entities" : qUnion([Q0, Q1, Q2, Q3, Q4, Q5, Q6, Q7, Q8, Q9, Q10, Q11, Q12, Q13, Q14, Q15, Q16, Q17, Q18, Q19, Q20, Q21, Q22, Q23, Q24, Q25, Q26, Q27, Q28, Q29, Q30, Q31, Q32, Q33, Q34, Q35, Q36]), "radius" : 2 * mm, "tangentPropagation" : true, "allowEdgeOverflow" : false});
        }
        {
            var Q0;
            Q0=makeQuery(id+"F5.boolean.opBoolean","COPY",EDGE,{"derivedFrom":makeQuery(id+"F5.opExtrude","SWEPT_EDGE",EDGE,{"disambiguationData":[OSD([sQuery(id+"F4.wireOp",EDGE,"E12"),sQuery(id+"F4.wireOp",EDGE,"E18")])]})});
            var Q1;
            Q1=makeQuery(id+"F5.boolean.opBoolean","COPY",EDGE,{"derivedFrom":makeQuery(id+"F5.opExtrude","SWEPT_EDGE",EDGE,{"disambiguationData":[OSD([sQuery(id+"F4.wireOp",EDGE,"E12"),sQuery(id+"F4.wireOp",EDGE,"E17")])]})});
            var Q2;
            Q2=makeQuery(id+"F5.boolean.opBoolean","COPY",EDGE,{"derivedFrom":makeQuery(id+"F5.opExtrude","SWEPT_EDGE",EDGE,{"disambiguationData":[OSD([sQuery(id+"F4.wireOp",EDGE,"E12"),sQuery(id+"F4.wireOp",EDGE,"E29")])]})});
            fillet(context, id + "F15", {"entities" : qUnion([Q0, Q1, Q2]), "radius" : 1 * mm, "tangentPropagation" : true, "allowEdgeOverflow" : false});
        }
        {
            var Q0;
            Q0=makeQuery(id+"F15.opFillet","BLEND_EDGE",EDGE,{"blendedFrom":[makeQuery(id+"F5.boolean.opBoolean","COPY",EDGE,{"derivedFrom":makeQuery(id+"F5.opExtrude","SWEPT_EDGE",EDGE,{"disambiguationData":[OSD([sQuery(id+"F4.wireOp",EDGE,"E12"),sQuery(id+"F4.wireOp",EDGE,"E29")])]})}),makeQuery(id+"F5.boolean.opBoolean","COPY",FACE,{"derivedFrom":makeQuery(id+"F5.opExtrude","SWEPT_FACE",FACE,{"disambiguationData":[OSD([sQuery(id+"F4.wireOp",EDGE,"E13")])]})})],"blendedInto":[makeQuery(id+"F5.boolean.opBoolean","COPY",FACE,{"derivedFrom":makeQuery(id+"F5.opExtrude","SWEPT_FACE",FACE,{"disambiguationData":[OSD([sQuery(id+"F4.wireOp",EDGE,"E13")])]})})]});
            fillet(context, id + "F16", {"entities" : qUnion([Q0]), "radius" : 1 * mm, "tangentPropagation" : true, "allowEdgeOverflow" : false});
        }
        {
            var Q0;
            {var subQ0=sQuery(id+"F4.wireOp",EDGE,"E12");Q0=makeQuery(id+"F5.boolean.opBoolean","COPY",EDGE,{"derivedFrom":makeQuery(id+"F5.opExtrude","CAP_EDGE",EDGE,{"disambiguationData":[OSD([subQ0]),TDD([makeQuery(id+"F4.imprint","IMPRINT",EDGE,{"disambiguationData":[TD([[makeQuery(id+"F4.imprint","INTERSECT",VERTEX,{"derivedFrom":[subQ0,sQuery(id+"F4.wireOp",EDGE,"E16")]}),1.0]])],"derivedFrom":subQ0})])],"isStart":false})});}
            var Q1;
            {var subQ0=sQuery(id+"F4.wireOp",EDGE,"E12");Q1=makeQuery(id+"F5.boolean.opBoolean","COPY",EDGE,{"derivedFrom":makeQuery(id+"F5.opExtrude","CAP_EDGE",EDGE,{"disambiguationData":[OSD([subQ0]),TDD([makeQuery(id+"F4.imprint","IMPRINT",EDGE,{"disambiguationData":[TD([[makeQuery(id+"F4.imprint","INTERSECT",VERTEX,{"derivedFrom":[subQ0,sQuery(id+"F4.wireOp",EDGE,"E17")]}),-1.0]])],"derivedFrom":subQ0})])],"isStart":false})});}
            var Q2;
            {var subQ0=sQuery(id+"F4.wireOp",EDGE,"E19");Q2=makeQuery(id+"F5.boolean.opBoolean","COPY",EDGE,{"derivedFrom":makeQuery(id+"F5.opExtrude","CAP_EDGE",EDGE,{"disambiguationData":[OSD([subQ0]),TDD([makeQuery(id+"F4.imprint","IMPRINT",EDGE,{"disambiguationData":[TD([[makeQuery(id+"F4.imprint","INTERSECT",VERTEX,{"derivedFrom":[sQuery(id+"F4.wireOp",EDGE,"E12"),subQ0]}),1.0]])],"derivedFrom":subQ0})])],"isStart":false})});}
            var Q3;
            Q3=makeQuery(id+"F5.boolean.opBoolean","COPY",EDGE,{"derivedFrom":makeQuery(id+"F5.opExtrude","CAP_EDGE",EDGE,{"disambiguationData":[OSD([sQuery(id+"F4.wireOp",EDGE,"E13")])],"isStart":false})});
            var Q4;
            {var subQ0=sQuery(id+"F4.wireOp",EDGE,"E21");Q4=makeQuery(id+"F5.boolean.opBoolean","COPY",EDGE,{"derivedFrom":makeQuery(id+"F5.opExtrude","CAP_EDGE",EDGE,{"disambiguationData":[OSD([subQ0]),TDD([makeQuery(id+"F4.imprint","IMPRINT",EDGE,{"disambiguationData":[TD([[makeQuery(id+"F4.imprint","INTERSECT",VERTEX,{"derivedFrom":[sQuery(id+"F4.wireOp",EDGE,"E18"),subQ0]}),1.0]])],"derivedFrom":subQ0})])],"isStart":false})});}
            var Q5;
            {var subQ0=sQuery(id+"F4.wireOp",EDGE,"E19");Q5=makeQuery(id+"F5.boolean.opBoolean","COPY",EDGE,{"derivedFrom":makeQuery(id+"F5.opExtrude","CAP_EDGE",EDGE,{"disambiguationData":[OSD([subQ0]),TDD([makeQuery(id+"F4.imprint","IMPRINT",EDGE,{"disambiguationData":[TD([[makeQuery(id+"F4.imprint","INTERSECT",VERTEX,{"derivedFrom":[sQuery(id+"F4.wireOp",EDGE,"E16"),subQ0]}),1.0]])],"derivedFrom":subQ0})])],"isStart":false})});}
            var Q6;
            {var subQ0=sQuery(id+"F4.wireOp",EDGE,"E21");Q6=makeQuery(id+"F5.boolean.opBoolean","COPY",EDGE,{"derivedFrom":makeQuery(id+"F5.opExtrude","CAP_EDGE",EDGE,{"disambiguationData":[OSD([subQ0]),TDD([makeQuery(id+"F4.imprint","IMPRINT",EDGE,{"disambiguationData":[TD([[makeQuery(id+"F4.imprint","INTERSECT",VERTEX,{"derivedFrom":[sQuery(id+"F4.wireOp",EDGE,"E19"),subQ0]}),-1.0]])],"derivedFrom":subQ0})])],"isStart":false})});}
            var Q7;
            {var subQ0=sQuery(id+"F4.wireOp",EDGE,"E23");Q7=makeQuery(id+"F5.boolean.opBoolean","COPY",EDGE,{"derivedFrom":makeQuery(id+"F5.opExtrude","CAP_EDGE",EDGE,{"disambiguationData":[OSD([subQ0]),TDD([makeQuery(id+"F4.imprint","IMPRINT",EDGE,{"disambiguationData":[TD([[makeQuery(id+"F4.imprint","INTERSECT",VERTEX,{"derivedFrom":[sQuery(id+"F4.wireOp",EDGE,"E16"),subQ0]}),-1.0]])],"derivedFrom":subQ0})])],"isStart":false})});}
            var Q8;
            {var subQ0=sQuery(id+"F4.wireOp",EDGE,"E23");Q8=makeQuery(id+"F5.boolean.opBoolean","COPY",EDGE,{"derivedFrom":makeQuery(id+"F5.opExtrude","CAP_EDGE",EDGE,{"disambiguationData":[OSD([subQ0]),TDD([makeQuery(id+"F4.imprint","IMPRINT",EDGE,{"disambiguationData":[TD([[makeQuery(id+"F4.imprint","INTERSECT",VERTEX,{"derivedFrom":[sQuery(id+"F4.wireOp",EDGE,"E17"),subQ0]}),1.0]])],"derivedFrom":subQ0})])],"isStart":false})});}
            var Q9;
            Q9=makeQuery(id+"F5.boolean.opBoolean","COPY",EDGE,{"derivedFrom":makeQuery(id+"F5.opExtrude","CAP_EDGE",EDGE,{"disambiguationData":[OSD([sQuery(id+"F4.wireOp",EDGE,"E13")])],"isStart":true})});
            var Q10;
            {var subQ0=sQuery(id+"F4.wireOp",EDGE,"E19");Q10=makeQuery(id+"F5.boolean.opBoolean","COPY",EDGE,{"derivedFrom":makeQuery(id+"F5.opExtrude","CAP_EDGE",EDGE,{"disambiguationData":[OSD([subQ0]),TDD([makeQuery(id+"F4.imprint","IMPRINT",EDGE,{"disambiguationData":[TD([[makeQuery(id+"F4.imprint","INTERSECT",VERTEX,{"derivedFrom":[sQuery(id+"F4.wireOp",EDGE,"E12"),subQ0]}),1.0]])],"derivedFrom":subQ0})])],"isStart":true})});}
            var Q11;
            {var subQ0=sQuery(id+"F4.wireOp",EDGE,"E12");Q11=makeQuery(id+"F5.boolean.opBoolean","COPY",EDGE,{"derivedFrom":makeQuery(id+"F5.opExtrude","CAP_EDGE",EDGE,{"disambiguationData":[OSD([subQ0]),TDD([makeQuery(id+"F4.imprint","IMPRINT",EDGE,{"disambiguationData":[TD([[makeQuery(id+"F4.imprint","INTERSECT",VERTEX,{"derivedFrom":[subQ0,sQuery(id+"F4.wireOp",EDGE,"E17")]}),-1.0]])],"derivedFrom":subQ0})])],"isStart":true})});}
            var Q12;
            {var subQ0=sQuery(id+"F4.wireOp",EDGE,"E12");Q12=makeQuery(id+"F5.boolean.opBoolean","COPY",EDGE,{"derivedFrom":makeQuery(id+"F5.opExtrude","CAP_EDGE",EDGE,{"disambiguationData":[OSD([subQ0]),TDD([makeQuery(id+"F4.imprint","IMPRINT",EDGE,{"disambiguationData":[TD([[makeQuery(id+"F4.imprint","INTERSECT",VERTEX,{"derivedFrom":[subQ0,sQuery(id+"F4.wireOp",EDGE,"E16")]}),1.0]])],"derivedFrom":subQ0})])],"isStart":true})});}
            var Q13;
            {var subQ0=sQuery(id+"F4.wireOp",EDGE,"E23");Q13=makeQuery(id+"F5.boolean.opBoolean","COPY",EDGE,{"derivedFrom":makeQuery(id+"F5.opExtrude","CAP_EDGE",EDGE,{"disambiguationData":[OSD([subQ0]),TDD([makeQuery(id+"F4.imprint","IMPRINT",EDGE,{"disambiguationData":[TD([[makeQuery(id+"F4.imprint","INTERSECT",VERTEX,{"derivedFrom":[sQuery(id+"F4.wireOp",EDGE,"E17"),subQ0]}),1.0]])],"derivedFrom":subQ0})])],"isStart":true})});}
            var Q14;
            {var subQ0=sQuery(id+"F4.wireOp",EDGE,"E23");Q14=makeQuery(id+"F5.boolean.opBoolean","COPY",EDGE,{"derivedFrom":makeQuery(id+"F5.opExtrude","CAP_EDGE",EDGE,{"disambiguationData":[OSD([subQ0]),TDD([makeQuery(id+"F4.imprint","IMPRINT",EDGE,{"disambiguationData":[TD([[makeQuery(id+"F4.imprint","INTERSECT",VERTEX,{"derivedFrom":[sQuery(id+"F4.wireOp",EDGE,"E16"),subQ0]}),-1.0]])],"derivedFrom":subQ0})])],"isStart":true})});}
            var Q15;
            {var subQ0=sQuery(id+"F4.wireOp",EDGE,"E16");Q15=makeQuery(id+"F5.boolean.opBoolean","COPY",EDGE,{"derivedFrom":makeQuery(id+"F5.opExtrude","CAP_EDGE",EDGE,{"disambiguationData":[OSD([subQ0]),TDD([makeQuery(id+"F4.imprint","IMPRINT",EDGE,{"disambiguationData":[TD([[makeQuery(id+"F4.imprint","INTERSECT",VERTEX,{"derivedFrom":[subQ0,sQuery(id+"F4.wireOp",EDGE,"E22")]}),-1.0]])],"derivedFrom":subQ0})])],"isStart":true})});}
            var Q16;
            {var subQ0=sQuery(id+"F4.wireOp",EDGE,"E21");Q16=makeQuery(id+"F5.boolean.opBoolean","COPY",EDGE,{"derivedFrom":makeQuery(id+"F5.opExtrude","CAP_EDGE",EDGE,{"disambiguationData":[OSD([subQ0]),TDD([makeQuery(id+"F4.imprint","IMPRINT",EDGE,{"disambiguationData":[TD([[makeQuery(id+"F4.imprint","INTERSECT",VERTEX,{"derivedFrom":[sQuery(id+"F4.wireOp",EDGE,"E18"),subQ0]}),1.0]])],"derivedFrom":subQ0})])],"isStart":true})});}
            var Q17;
            {var subQ0=sQuery(id+"F4.wireOp",EDGE,"E21");Q17=makeQuery(id+"F5.boolean.opBoolean","COPY",EDGE,{"derivedFrom":makeQuery(id+"F5.opExtrude","CAP_EDGE",EDGE,{"disambiguationData":[OSD([subQ0]),TDD([makeQuery(id+"F4.imprint","IMPRINT",EDGE,{"disambiguationData":[TD([[makeQuery(id+"F4.imprint","INTERSECT",VERTEX,{"derivedFrom":[sQuery(id+"F4.wireOp",EDGE,"E19"),subQ0]}),-1.0]])],"derivedFrom":subQ0})])],"isStart":true})});}
            var Q18;
            Q18=makeQuery(id+"F1.opExtrude","CAP_EDGE",EDGE,{"disambiguationData":[OSD([sQuery(id+"F0.wireOp",EDGE,"E9")])],"isStart":true});
            var Q19;
            Q19=makeQuery(id+"F8.opChamfer","BLEND_EDGE",EDGE,{"blendedFrom":[makeQuery(id+"F1.opExtrude","CAP_EDGE",EDGE,{"disambiguationData":[OSD([sQuery(id+"F0.wireOp",EDGE,"E0")])],"isStart":true}),makeQuery(id+"F1.opExtrude","SWEPT_FACE",FACE,{"disambiguationData":[OSD([sQuery(id+"F0.wireOp",EDGE,"E9")])]})],"blendedInto":[makeQuery(id+"F1.opExtrude","SWEPT_FACE",FACE,{"disambiguationData":[OSD([sQuery(id+"F0.wireOp",EDGE,"E9")])]})]});
            var Q20;
            {var subQ0=sQuery(id+"F0.wireOp",EDGE,"E0");Q20=makeQuery(id+"F9.opFillet","BLEND_EDGE",EDGE,{"blendedFrom":[makeQuery(id+"F8.opChamfer","BLEND_EDGE",EDGE,{"blendedFrom":[makeQuery(id+"F1.opExtrude","CAP_EDGE",EDGE,{"disambiguationData":[OSD([subQ0])],"isStart":true}),makeQuery(id+"F1.opExtrude","SWEPT_FACE",FACE,{"disambiguationData":[OSD([subQ0])]})],"blendedInto":[makeQuery(id+"F1.opExtrude","SWEPT_FACE",FACE,{"disambiguationData":[OSD([subQ0])]})]}),makeQuery(id+"F1.opExtrude","SWEPT_FACE",FACE,{"disambiguationData":[OSD([sQuery(id+"F0.wireOp",EDGE,"E9")])]})],"blendedInto":[makeQuery(id+"F1.opExtrude","SWEPT_FACE",FACE,{"disambiguationData":[OSD([sQuery(id+"F0.wireOp",EDGE,"E9")])]})]});}
            chamfer(context, id + "F17", {"entities" : qUnion([Q0, Q1, Q2, Q3, Q4, Q5, Q6, Q7, Q8, Q9, Q10, Q11, Q12, Q13, Q14, Q15, Q16, Q17, Q18, Q19, Q20]), "width" : 1 * mm, "tangentPropagation" : true});
        }
    });
